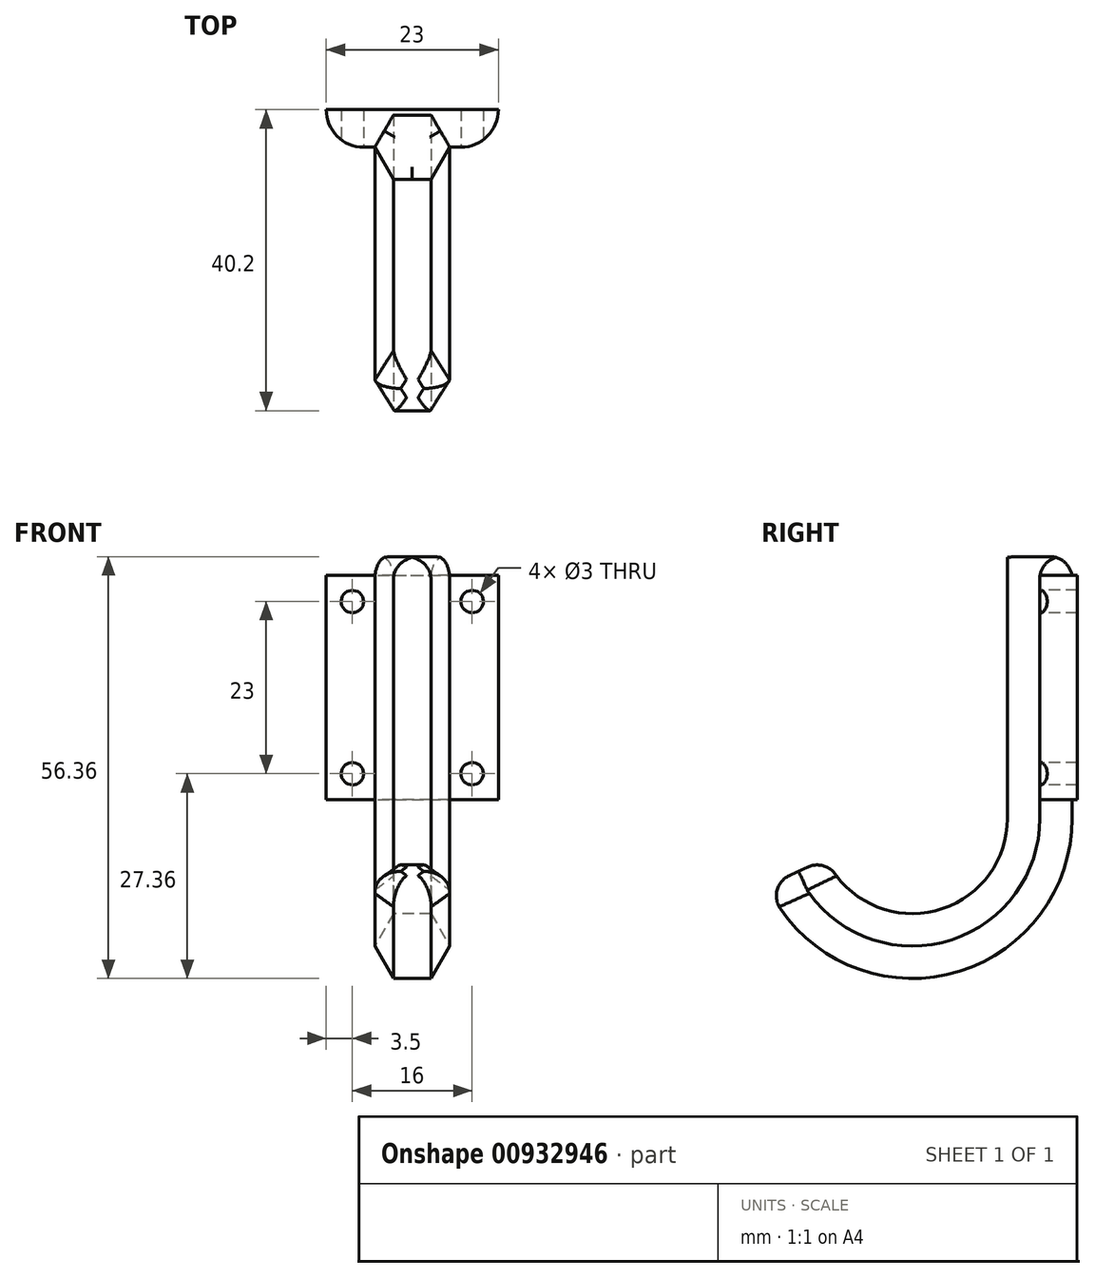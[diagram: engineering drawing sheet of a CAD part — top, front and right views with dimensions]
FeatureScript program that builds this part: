
annotation { "Feature Type Name" : "Feature", "Feature Type Description" : "" }
export const myFeature = defineFeature(function(context is Context, id is Id, definition is map)
    precondition{}
    {
        {
            var Q0;
            Q0=qCreatedBy(makeId("Right.planeOp"),FACE);
            var sketch = newSketch(context, id + "F0", { "sketchPlane" : qUnion([Q0])});
            skLineSegment(sketch, "E0", {"start": v(0, 0) * mm, "end": v(0, -35) * mm});
            skArc(sketch, "E1", {"start": v(-32.48, -42.16) * mm, "mid": v(-13.36, -51.63) * mm, "end": v(0, -35) * mm});
            skSolve(sketch);
        }
        {
            var Q0;
            Q0=qCreatedBy(makeId("Top.planeOp"),FACE);
            var sketch = newSketch(context, id + "F1", { "sketchPlane" : qUnion([Q0])});
            skCircle(sketch, "E2.cCircle", {"center": v(0, 0) * mm, "radius": 5 * mm, "construction": true});
            skLineSegment(sketch, "E2.0", {"start": v(5, 0) * mm, "end": v(2.5, -4.33) * mm});
            skLineSegment(sketch, "E2.1", {"start": v(2.5, -4.33) * mm, "end": v(-2.5, -4.33) * mm});
            skLineSegment(sketch, "E2.2", {"start": v(-2.5, -4.33) * mm, "end": v(-5, 0) * mm});
            skLineSegment(sketch, "E2.3", {"start": v(-5, 0) * mm, "end": v(-2.5, 4.33) * mm});
            skLineSegment(sketch, "E2.4", {"start": v(-2.5, 4.33) * mm, "end": v(2.5, 4.33) * mm});
            skLineSegment(sketch, "E2.5", {"start": v(2.5, 4.33) * mm, "end": v(5, 0) * mm});
            skSolve(sketch);
        }
        {
            var Q0;
            Q0=makeQuery(id+"F1.imprint","IMPRINT",FACE,{"disambiguationData":[TD([[makeQuery(id+"F1.imprint","IMPRINT",EDGE,{"derivedFrom":sQuery(id+"F1.wireOp",EDGE,"E2.0")}),-1.0]])]});
            var Q1;
            Q1=sQuery(id+"F0.wireOp",EDGE,"E0");
            var Q2;
            Q2=sQuery(id+"F0.wireOp",EDGE,"E1");
            sweep(context, id + "F2", {"profiles" : qUnion([Q0]), "path" : qUnion([Q1, Q2])});
        }
        {
            var Q0;
            Q0=makeQuery(id+"F2.opSweep","CAP_FACE",FACE,{"disambiguationData":[OSD([sQuery(id+"F0.wireOp",VERTEX,"E1.start"),sQuery(id+"F1.wireOp",EDGE,"E2.0"),sQuery(id+"F1.wireOp",EDGE,"E2.1"),sQuery(id+"F1.wireOp",EDGE,"E2.2"),sQuery(id+"F1.wireOp",EDGE,"E2.3"),sQuery(id+"F1.wireOp",EDGE,"E2.4"),sQuery(id+"F1.wireOp",EDGE,"E2.5")])],"isStart":false});
            var Q1;
            Q1=makeQuery(id+"F2.opSweep","CAP_EDGE",EDGE,{"disambiguationData":[OSD([sQuery(id+"F0.wireOp",VERTEX,"E0.start"),sQuery(id+"F1.wireOp",EDGE,"E2.2")])],"isStart":true});
            var Q2;
            Q2=makeQuery(id+"F2.opSweep","CAP_EDGE",EDGE,{"disambiguationData":[OSD([sQuery(id+"F0.wireOp",VERTEX,"E0.start"),sQuery(id+"F1.wireOp",EDGE,"E2.0")])],"isStart":true});
            var Q3;
            Q3=makeQuery(id+"F2.opSweep","CAP_EDGE",EDGE,{"disambiguationData":[OSD([sQuery(id+"F0.wireOp",VERTEX,"E0.start"),sQuery(id+"F1.wireOp",EDGE,"E2.4")])],"isStart":true});
            fillet(context, id + "F3", {"entities" : qUnion([Q0, Q1, Q2, Q3]), "radius" : 3 * mm, "tangentPropagation" : true, "allowEdgeOverflow" : false});
        }
        {
            var Q0;
            Q0=qCreatedBy(makeId("Front.planeOp"),FACE);
            var sketch = newSketch(context, id + "F4", { "sketchPlane" : qUnion([Q0])});
            skLineSegment(sketch, "E3.bottom", {"start": v(-11.5, -2.5) * mm, "end": v(11.5, -2.5) * mm});
            skLineSegment(sketch, "E3.top", {"start": v(-11.5, -32.5) * mm, "end": v(11.5, -32.5) * mm});
            skLineSegment(sketch, "E3.left", {"start": v(-11.5, -2.5) * mm, "end": v(-11.5, -32.5) * mm});
            skLineSegment(sketch, "E3.right", {"start": v(11.5, -2.5) * mm, "end": v(11.5, -32.5) * mm});
            skPoint(sketch, "E3.middle", {"position": v(0, -17.5) * mm});
            skCircle(sketch, "E4", {"center": v(8, -6) * mm, "radius": 1.5 * mm});
            skCircle(sketch, "E5.0.1.0", {"center": v(8, -29) * mm, "radius": 1.5 * mm});
            skCircle(sketch, "E5.1.0.0", {"center": v(-8, -6) * mm, "radius": 1.5 * mm});
            skCircle(sketch, "E5.1.1.0", {"center": v(-8, -29) * mm, "radius": 1.5 * mm});
            skLineSegment(sketch, "E5.direction1", {"start": v(8, -6) * mm, "end": v(-8, -6) * mm, "construction": true});
            skLineSegment(sketch, "E5.direction2", {"start": v(8, -6) * mm, "end": v(8, -29) * mm, "construction": true});
            skSolve(sketch);
        }
        {
            var Q0;
            Q0=makeQuery(id+"F4.imprint","IMPRINT",FACE,{"disambiguationData":[TD([[makeQuery(id+"F4.imprint","IMPRINT",EDGE,{"derivedFrom":sQuery(id+"F4.wireOp",EDGE,"E3.bottom")}),-1.0]])]});
            extrude(context, id + "F5", {"entities" : qUnion([Q0]), "operationType" : NewBodyOperationType.ADD, "oppositeDirection" : true, "depth" : 5 * mm, "offsetDistance" : 25 * mm});
        }
        {
            var Q0;
            Q0=makeQuery(id+"F5.opExtrude","CAP_EDGE",EDGE,{"disambiguationData":[OSD([sQuery(id+"F4.wireOp",EDGE,"E3.right")])],"isStart":true});
            var Q1;
            Q1=makeQuery(id+"F5.opExtrude","CAP_EDGE",EDGE,{"disambiguationData":[OSD([sQuery(id+"F4.wireOp",EDGE,"E3.left")])],"isStart":true});
            fillet(context, id + "F6", {"entities" : qUnion([Q0, Q1]), "radius" : 5 * mm, "tangentPropagation" : true, "allowEdgeOverflow" : false});
        }
    });
